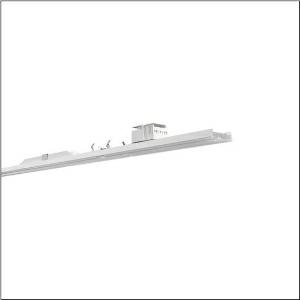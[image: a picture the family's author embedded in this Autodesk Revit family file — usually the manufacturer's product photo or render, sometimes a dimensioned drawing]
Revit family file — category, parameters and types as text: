
# Revit family: licross_r__11_recessed_mo_51tl19dn49xfd_398d
name_source: partatom
category: Lighting Fixtures
units: mm (PartAtom-declared; Revit-internal decimal feet)

## family parameters
Cut with Voids When Loaded = No
Host = Face
Light Source = No
Part Type = Normal
Room Calculation Point = No
Round Connector Dimension = Use Diameter
Shared = No

## types (1)
- --- (1 x LED, 1430 lm, 10 W, 4000K)
    Apparent Load = 10 VA
    CIE Flux Codes = 55 90 98 100 100
    Color Rendering = 80
    Color Temperature = 4000K
    Default Elevation = 1800 mm
    Description = Licross® 11 Recessed MOluminaire insert, length: 1.500mm, width: 66mm, height: 67mm, LED rated luminous flux: 9.010lm, light colour: 840, control gear: DALI 2, control gear: ECG DALI, with plug, 6-pole, with phase selection, mains connection: 220..240V, AC/DC, 0/50..60Hz, without changeover relay, for emergency light function, for central battery installations according to DIN EN 60598-2-22, halogen-free wiring, primary light control with lens, of plastic, primary optical cover: cover, of PMMA, light emission: direct distribution, primary light characteristic: double asymmetric, protection rating (complete): IP40, insulation class (complete): insulation class I (protective earthing), certification: CE, ENEC, VDE, protection symbol: D if used in an environment without relevant dust loads with corresponding accessories, permissible ambient temperature for indoor applications: -25..+35°C, standard: EN 60598-2-22, reducing of maximum allowable ambient temperature of 5°C with ceiling mounting, corresponds to IFS (International Featured Standards) requirements for safety and quality in the food industry, packaging unit: 1 piece
    Height = 58 mm
    Lamp = 1 x LED
    Lamp Light Flux = 1430 lm
    Lamp Power = 10 W
    Lamp count = 1
    Length = 1500 mm
    Luminous efficacy = 143 lm/W
    Manufacturer = Siteco
    ModVariant = No
    Model = 51TL19DN49XFD
    Mounting Place = Ceiling
    Mounting Type = Pendant
    Number of Poles = 1
    OnlyDefault = Yes
    Power Factor = 1
    Product Name = Licross® 11 Recessed MO
    Product group = luminaire insert
    ProductGroupID = 902
    Protection Class = Protection class I
    Protection Degree = IP 40
    RLX_Detail_Level = 1
    RlxData = <blob elided: 22673 chars, md5=0689fb7c>
    Socket = socket
    Standby Power = 0 W
    System Light Flux = 1430 lm
    System Power = 10 W
    Type Comments = : DC mode (central or group accumulator) initial emergency light level
    Type Image = l_1266722.jpg
    URL = http://relux.com
    VarID = @adj_134469
    Voltage = 0 V
    Weight = 0.00 kg
    Width = 66 mm

## geometry (parser evidence)
native form markers: Blend x4, Sweep x10
no freeform markers — native parametric forms only
